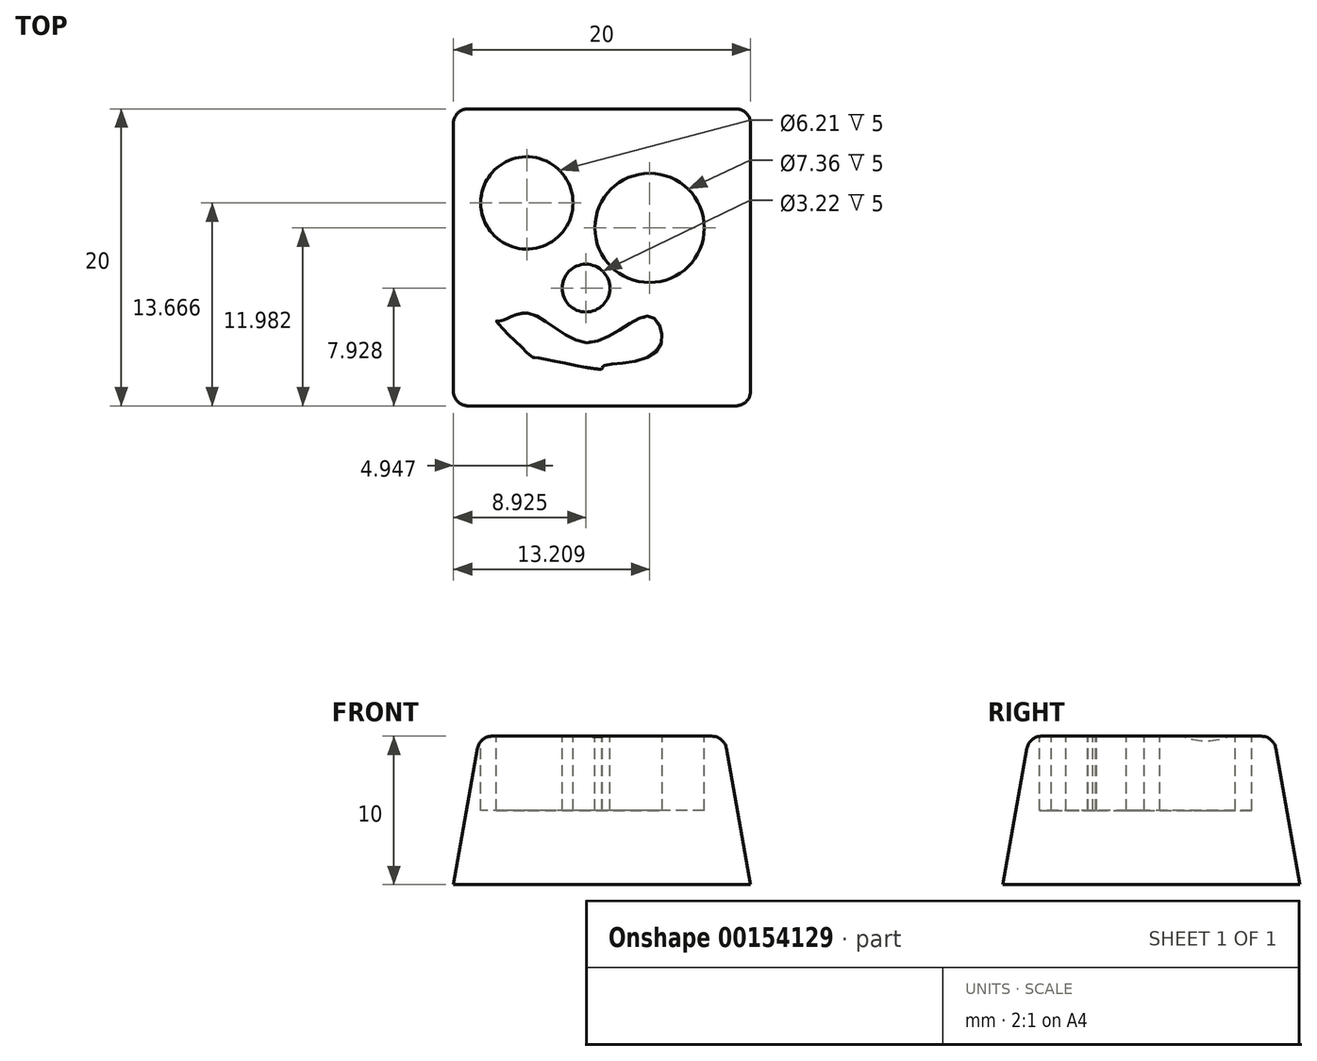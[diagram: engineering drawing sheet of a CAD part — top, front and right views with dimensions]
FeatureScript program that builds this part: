
annotation { "Feature Type Name" : "Feature", "Feature Type Description" : "" }
export const myFeature = defineFeature(function(context is Context, id is Id, definition is map)
    precondition{}
    {
        {
            var Q0;
            Q0=qCreatedBy(makeId("Top.planeOp"),FACE);
            var sketch = newSketch(context, id + "F0", { "sketchPlane" : qUnion([Q0])});
            skLineSegment(sketch, "E0.bottom", {"start": v(10, 10) * mm, "end": v(-10, 10) * mm});
            skLineSegment(sketch, "E0.top", {"start": v(10, -10) * mm, "end": v(-10, -10) * mm});
            skLineSegment(sketch, "E0.left", {"start": v(10, 10) * mm, "end": v(10, -10) * mm});
            skLineSegment(sketch, "E0.right", {"start": v(-10, 10) * mm, "end": v(-10, -10) * mm});
            skPoint(sketch, "E0.middle", {"position": v(0, 0) * mm});
            skSolve(sketch);
        }
        {
            var Q0;
            Q0 = qSketchRegion(id + "F0", true);
            extrude(context, id + "F1", {"entities" : qUnion([Q0]), "depth" : 10 * mm, "hasDraft" : true, "draftAngle" : 10 * degree, "draftPullDirection" : true});
        }
        {
            var Q0;
            Q0=makeQuery(id+"F1.opExtrude","CAP_FACE",FACE,{"disambiguationData":[OSD([sQuery(id+"F0.wireOp",EDGE,"E0.bottom"),sQuery(id+"F0.wireOp",EDGE,"E0.top"),sQuery(id+"F0.wireOp",EDGE,"E0.left"),sQuery(id+"F0.wireOp",EDGE,"E0.right")])],"isStart":false});
            var sketch = newSketch(context, id + "F2", { "sketchPlane" : qUnion([Q0])});
            skCircle(sketch, "E1", {"center": v(-5.05, 3.67) * mm, "radius": 3.1 * mm});
            skCircle(sketch, "E2", {"center": v(3.2, 1.98) * mm, "radius": 3.68 * mm});
            skCircle(sketch, "E3", {"center": v(-1.08, -2.07) * mm, "radius": 1.6 * mm});
            skFitSpline(sketch, "E4", {"points": [v(-4.98, -3.76) * mm, v(-0.85, -5.74) * mm, v(3.29, -3.98) * mm, v(3.67, -6.36) * mm, v(0, -7.35) * mm, v(0, -7.5) * mm, v(-4.6, -6.74) * mm, v(-4.67, -6.74) * mm, v(-7.12, -4.3) * mm, v(-6.89, -4.3) * mm, v(-4.98, -3.76) * mm]});
            skSolve(sketch);
        }
        {
            var Q0;
            Q0 = qSketchRegion(id + "F2", true);
            extrude(context, id + "F3", {"entities" : qUnion([Q0]), "operationType" : NewBodyOperationType.REMOVE, "oppositeDirection" : true, "depth" : 5 * mm});
        }
        {
            var Q0;
            Q0=makeQuery(id+"F1.opExtrude","CAP_EDGE",EDGE,{"disambiguationData":[OSD([sQuery(id+"F0.wireOp",EDGE,"E0.bottom")])],"isStart":false});
            var Q1;
            Q1=makeQuery(id+"F1.opExtrude","CAP_EDGE",EDGE,{"disambiguationData":[OSD([sQuery(id+"F0.wireOp",EDGE,"E0.left")])],"isStart":false});
            var Q2;
            Q2=makeQuery(id+"F1.opExtrude","CAP_EDGE",EDGE,{"disambiguationData":[OSD([sQuery(id+"F0.wireOp",EDGE,"E0.top")])],"isStart":false});
            var Q3;
            Q3=makeQuery(id+"F1.opExtrude","CAP_EDGE",EDGE,{"disambiguationData":[OSD([sQuery(id+"F0.wireOp",EDGE,"E0.right")])],"isStart":false});
            var Q4;
            Q4=makeQuery(id+"F1.opExtrude","SWEPT_EDGE",EDGE,{"disambiguationData":[OSD([sQuery(id+"F0.wireOp",EDGE,"E0.bottom"),sQuery(id+"F0.wireOp",EDGE,"E0.right")])]});
            var Q5;
            Q5=makeQuery(id+"F1.opExtrude","SWEPT_EDGE",EDGE,{"disambiguationData":[OSD([sQuery(id+"F0.wireOp",EDGE,"E0.bottom"),sQuery(id+"F0.wireOp",EDGE,"E0.left")])]});
            var Q6;
            Q6=makeQuery(id+"F1.opExtrude","SWEPT_EDGE",EDGE,{"disambiguationData":[OSD([sQuery(id+"F0.wireOp",EDGE,"E0.top"),sQuery(id+"F0.wireOp",EDGE,"E0.right")])]});
            var Q7;
            Q7=makeQuery(id+"F1.opExtrude","SWEPT_EDGE",EDGE,{"disambiguationData":[OSD([sQuery(id+"F0.wireOp",EDGE,"E0.top"),sQuery(id+"F0.wireOp",EDGE,"E0.left")])]});
            fillet(context, id + "F4", {"entities" : qUnion([Q0, Q1, Q2, Q3, Q4, Q5, Q6, Q7]), "radius" : 1 * mm, "tangentPropagation" : true, "allowEdgeOverflow" : false});
        }
    });
